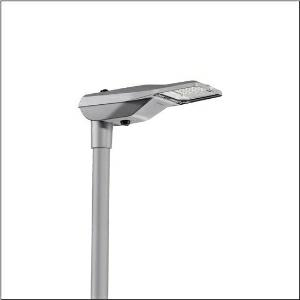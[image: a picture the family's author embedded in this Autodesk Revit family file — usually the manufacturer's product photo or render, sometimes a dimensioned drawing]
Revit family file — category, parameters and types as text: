
# Revit family: streetlight_sl_21_iq_micro___stw1_0a_5xe1e31y08cb_f1b3
name_source: partatom
category: Lighting Fixtures
units: mm (PartAtom-declared; Revit-internal decimal feet)

## family parameters
Cut with Voids When Loaded = No
Host = Face
Light Source = No
Part Type = Normal
Room Calculation Point = No
Round Connector Dimension = Use Diameter
Shared = No

## types (1)
- --- (1 x LED, 2880 lm, 19.1 W, 3000K)
    Apparent Load = 19 VA
    CIE Flux Codes = 38 75 98 100 100
    Color Rendering = 70
    Color Temperature = 3000K
    Default Elevation = 1800 mm
    Description = Streetlight SL 21 iQ micro, mast luminaire, primary light control with lens, of PMMA, primary optical cover: cover, of toughened safety glass, transparent, light distribution: STW1.0a, light emission: direct distribution, primary light characteristic: asymmetric, installation type: post-top, side-entry, LED, High Power LED, rated luminous flux: 2.880lm, luminous efficacy: 151lm/W, light colour: 730, colour temperature: 3000K, control gear: iQ-Street Remote, D4i with power reduction, control: pre-setting: logarithmic dimming characteristic, Street-Remote, Auto-Match, Temp-Guard, Lumen-Switch, Night-Set, Smart-Wire, Light-Fading, Desk-Remote (wireless, voltage-free reading and setting of iQ features in the workshop via application-optimized NFC function/RFID function), optimised constant luminous flux control (CLO 2.0), mains connection: 220..240V, AC, 50/60Hz, start of lifetime: 19W, end of service life: 20W, reduction: 9W, luminaire housing, of diecast aluminium, powder-coated, SITECO metallic grey (DB 702S), corrosivity category C5 high according to DIN EN ISO 12944, please order mast flange separately, inclination adjustable: 0°, 5°, 10°, 15°, sealing non-destructively replaceable, multi-level sealing system, length: 528mm, width: 235mm, height: 110mm, mast flange for spigot size: 42mm (side-entry): 5XC10008XM4, 60/48mm (side-entry/post-top): 5XC10108XM2, 76/60mm (side-entry/post-top): 5XC10108XM1, mounting height: 4..8m, Smart Interface below and above, protection rating (complete): IP66, insulation class (complete): insulation class II (safety insulation), certification: CE, ENEC, ENEC+, VDE, impact resistance: IK10, permissible operating ambient temperature for outdoor applications: -40..+50°C, standard-compliant lighting for roads and squares, packaging unit: 1 piece

Light Distribution: STW1.0a
    Height = 110 mm
    Lamp = 1 x LED
    Lamp Light Flux = 2880 lm
    Lamp Power = 19.1 W
    Lamp count = 1
    Length = 528 mm
    Luminous efficacy = 151 lm/W
    Manufacturer = Siteco
    ModVariant = No
    Model = 5XE1E31Y08CB
    Number of Poles = 1
    OnlyDefault = Yes
    Power Factor = 1
    Product Name = Streetlight SL 21 iQ micro | STW1.0a
    Product group = mast luminaire | pylon top
    ProductGroupID = 6100
    Protection Class = Protection class II
    Protection Degree = IP 66
    RLX_Detail_Level = 1
    RLX_Emergency_Light_Flux = 0 lm
    RLX_Emergency_Type = 0
    RLX_Emergency_Type_DB = No
    RlxData = <blob elided: 99293 chars, md5=1689a4fc>
    Socket = socket
    Standby Power = 0 W
    System Light Flux = 2880 lm
    System Power = 19 W
    Type Comments = factory setting: luminous flux: 100 % | dim-lin: 254 | 387 mA
    Type Image = l_1007239.jpg
    URL = http://relux.com
    VarID = @adj_114539
    Voltage = 0 V
    Weight = 0.00 kg
    Width = 235 mm

## geometry (parser evidence)
native form markers: Blend x4, Sweep x11
no freeform markers — native parametric forms only
